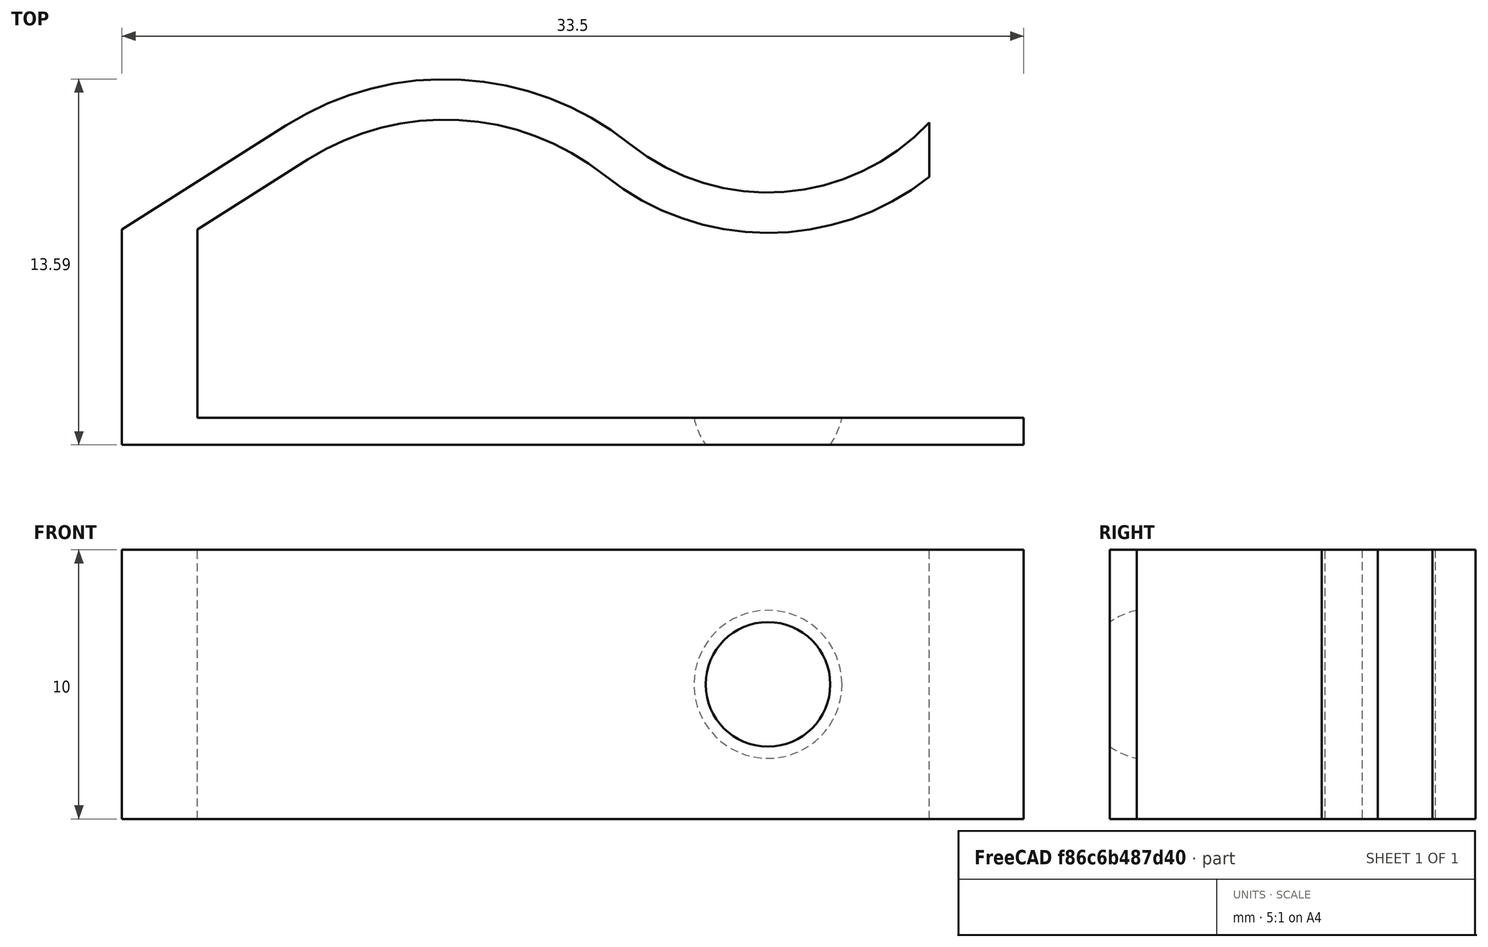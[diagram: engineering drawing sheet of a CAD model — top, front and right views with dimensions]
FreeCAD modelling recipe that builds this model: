
FCSTD DOCUMENT  (FreeCAD 0.16R5342 (Git))
Label: PS2LensHolder
License: All rights reserved
LicenseURL: http://en.wikipedia.org/wiki/All_rights_reserved
objects: Sketcher::SketchObject×2, Mesh::Feature×1, App::DocumentObjectGroup×1, PartDesign::Pad×1, Part::Revolution×1, Part::Cut×1, Part::Feature×1
note: 7 computed .brp shape members not serialized (recipe doc carries the construction recipe); baked Part::Feature solids carry a one-line shape summary decoded from their .brp

FEATURE [Mesh::Feature] _50Clip  label="350Clip"
  Placement = pos=(0,-2,0) rot=(0,0,1;0rad)
FEATURE [App::DocumentObjectGroup] Group  label="Reference"
  Group = -> [_50Clip]
FEATURE [Sketcher::SketchObject] Sketch  label="Base"
  sketch-geometry (14):
    g0: LineSegment StartX=0 StartY=8 StartZ=0 EndX=0 EndY=0 EndZ=0
    g1: LineSegment StartX=0 StartY=0 StartZ=0 EndX=33.5 EndY=0 EndZ=0
    g2: LineSegment StartX=33.5 StartY=0 StartZ=0 EndX=33.5 EndY=1 EndZ=0
    g3: LineSegment StartX=33.5 StartY=1 StartZ=0 EndX=2.8 EndY=1 EndZ=0
    g4: LineSegment StartX=2.8 StartY=1 StartZ=0 EndX=2.8 EndY=8 EndZ=0
    g5: LineSegment StartX=0 StartY=8 StartZ=0 EndX=6.10713 EndY=11.8746 EndZ=0
    g6: LineSegment StartX=2.8 StartY=8 StartZ=0 EndX=6.91071 EndY=10.608 EndZ=0
    g7: ArcOfCircle CenterX=12 CenterY=2.58618 CenterZ=0 NormalX=0 NormalY=0 NormalZ=1 Radius=11 StartAngle=0.896055 EndAngle=2.13615
    g8: ArcOfCircle CenterX=12 CenterY=2.58618 CenterZ=0 NormalX=0 NormalY=0 NormalZ=1 Radius=9.5 StartAngle=0.896055 EndAngle=2.13615
    g9: ArcOfCircle CenterX=24 CenterY=17.5862 CenterZ=0 NormalX=0 NormalY=0 NormalZ=1 Radius=9.70937 StartAngle=4.03765 EndAngle=5.37853
    g10: ArcOfCircle CenterX=24 CenterY=17.5862 CenterZ=0 NormalX=0 NormalY=0 NormalZ=1 Radius=8.20937 StartAngle=4.03765 EndAngle=5.53199
    g11: LineSegment StartX=30 StartY=11.9832 StartZ=0 EndX=30 EndY=9.95257 EndZ=0
    g12: LineSegment [constr] StartX=6.10713 StartY=11.8746 StartZ=0 EndX=6.91071 EndY=10.608 EndZ=0
    g13: LineSegment [constr] StartX=18.8716 StartY=11.1757 StartZ=0 EndX=17.9346 EndY=10.0044 EndZ=0
  constraints (42):
    c: Coincident(g0,g1)
    c: Coincident(g1,g2)
    c: Coincident(g2,g3)
    c: Coincident(g3,g4)
    c: Coincident(g0,g5)
    c: Coincident(g4,g6)
    c: Coincident(g7,g5)
    c: Coincident(g6,g8)
    c: Coincident(g8,g9)
    c: Coincident(g7,g10)
    c: Coincident(g9,g11)
    c: Coincident(g10,g11)
    c: Horizontal(g3)
    c: Horizontal(g1)
    c: Vertical(g2)
    c: Vertical(g4)
    c: Vertical(g0)
    c: Tangent(g7,g5)
    c: Tangent(g6,g8)
    c: Tangent(g7,g10)
    c: Tangent(g8,g9)
    c: Parallel(g6,g5)
    c: Coincident(g7,g8)
    c: Coincident(g9,g10)
    c: Vertical(g11)
    c: Coincident(g0,g-1)
    c: DistanceY(g2) = 1
    c: DistanceX(g1) = 33.5
    c: DistanceX(g0,g4) = 2.8
    c: DistanceY(g0) = 8
    c: DistanceY(g4,g0) = 0
    c: DistanceX(g9) = 30
    c: Coincident(g12,g6)
    c: Coincident(g12,g5)
    c: Coincident(g13,g8)
    c: Coincident(g13,g7)
    c: Equal(g12,g13)
    c: Distance(g12) = 1.5
    c: DistanceX(g7) = 12
    c: DistanceX(g7,g9) = 12
    c: DistanceY(g9,g7) = -15
    c: Radius(g7) = 11
FEATURE [PartDesign::Pad] Pad  label="Base001"
  Length = 10
  Length2 = 100
  Sketch = -> Sketch
  Type = 0
FEATURE [Sketcher::SketchObject] Sketch001  label="Sphere"
  sketch-geometry (3):
    g0: ArcOfCircle CenterX=0 CenterY=-0.605973 CenterZ=0 NormalX=0 NormalY=0 NormalZ=1 Radius=2.81597 StartAngle=1.5708 EndAngle=2.9247
    g1: LineSegment StartX=0 StartY=2.21 StartZ=0 EndX=0 EndY=0 EndZ=0
    g2: LineSegment StartX=0 StartY=0 StartZ=0 EndX=-2.75 EndY=0 EndZ=0
  constraints (9):
    c: PointOnObject(g0,g-1)
    c: PointOnObject(g0,g-2)
    c: Coincident(g2,g0)
    c: Coincident(g2,g-1)
    c: Coincident(g1,g-1)
    c: Coincident(g1,g0)
    c: DistanceY(g1) = -2.21
    c: DistanceX(g2) = -2.75
    c: PointOnObject(g0,g-2)
FEATURE [Part::Revolution] Revolve  label="Spherecut"
  Angle = 360
  Axis = (0,1,0)
  Base = (0,0,0)
  Placement = pos=(24,1,5) rot=(0,0,1;3.14159rad)
  Solid = true
  Source = -> Sketch001
FEATURE [Part::Cut] Cut  label="SphereCut"
  Base = -> Pad
  Tool = -> Revolve
FEATURE [Part::Feature] Cut001  label="PS2LensHolder"
  shape: bbox 33.5 x 13.59 x 10 mm, 15 faces (baked)
